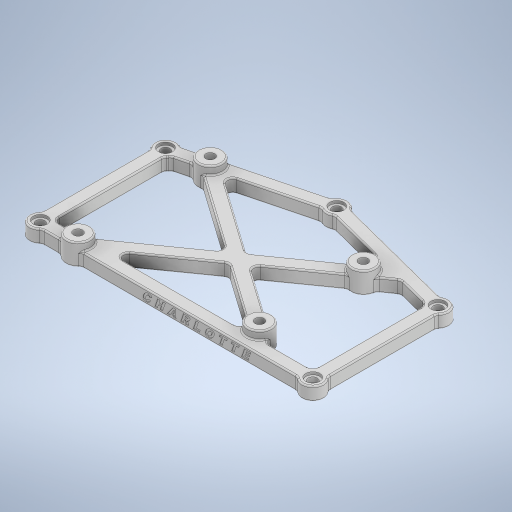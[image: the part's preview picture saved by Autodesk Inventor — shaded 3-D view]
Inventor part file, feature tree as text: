
AUTODESK INVENTOR PART (.ipt)
format: ipt  version: 2024.2 (Build 282272000, 272)  size: 1,391,104 bytes
history: native  units: mm
features: sketch x8, extrude x7, emboss x3, fillet x2, hole x1
ambient origin geometry x8: Origin, YZ Plane, XZ Plane, XY Plane, X Axis, Y Axis, Z Axis, Center Point
bodies: Solid1 (feature_tree)
feature tree (21):
  sketch  "Sketch1"  dims[d0=4.9mm d1=101.0mm]
  extrude  "Extrusion1"  Depth=4.9mm
  extrude  "Extrusion2"  Depth=50.5mm
  extrude  "Extrusion3"  Depth=8.0mm
  hole  "Hole1"  [1 undecoded]
  extrude  "Extrusion4"  Depth=62.0mm
  extrude  "Extrusion5"  Depth=5.0mm
  fillet  "Fillet1"  Radius=2.5mm
  fillet  "Fillet3"  Radius=5.0mm
  emboss  "Emboss1"
  emboss  "Emboss4"
  emboss  "Emboss5"
  extrude  "Extrusion6"  Depth=2.5mm
  extrude  "Extrusion7"  Depth=2.5mm
  sketch  "Sketch3"  dims[d2=13.0mm d3=50.5mm]
  sketch  "Sketch4"  dims[d4=8.0mm d6=49.0mm]
  sketch  "Sketch5"  dims[d7=46.4mm d8=5.25mm]
  sketch  "Sketch8"  dims[d9=5.25mm d10=62.0mm]
  sketch  "Sketch9"  dims[d12=9.0mm d13=5.0mm d14=2.5mm d21=5.0mm]
  sketch  "Sketch10"  dims[d22=2.5mm d23=2.5mm]
  sketch  "Sketch11"  dims[d30=5.0mm d31=2.5mm d32=2.5mm d33=5.0mm d35=2.5mm d38=3.4mm d39=5.0mm d40=2.5mm d41=2.5mm d42=5.0mm d43=5.0mm d44=2.5mm d45=2.5mm d46=2.5mm d47=2.5mm d48=5.0mm d49=0.0mm d52=8.0mm d53=0.0mm d54=1.9mm d55=0.0mm d56=3.4mm d57=6.0mm d58=4.0mm d59=2.0mm d60=90.0deg d61=8.0mm d62=20.594885mm d63=5.7mm d64=5.0mm d65=0.0mm d66=5.25mm d67=1.0mm d68=0.0mm d69=2.0mm d71=25.0mm d75=0.25mm d76=0.0mm d81=0.2mm d82=0.0mm d83=0.2mm d84=0.0mm d85=0.5mm d86=0.25mm d87=0.0mm d88=0.25mm d89=0.0mm]
note: 1 required parameter value undecoded (feature->parameter linkage not recoverable at this tier; creation-order binding heuristic only, values carry confidence <= 0.55)
